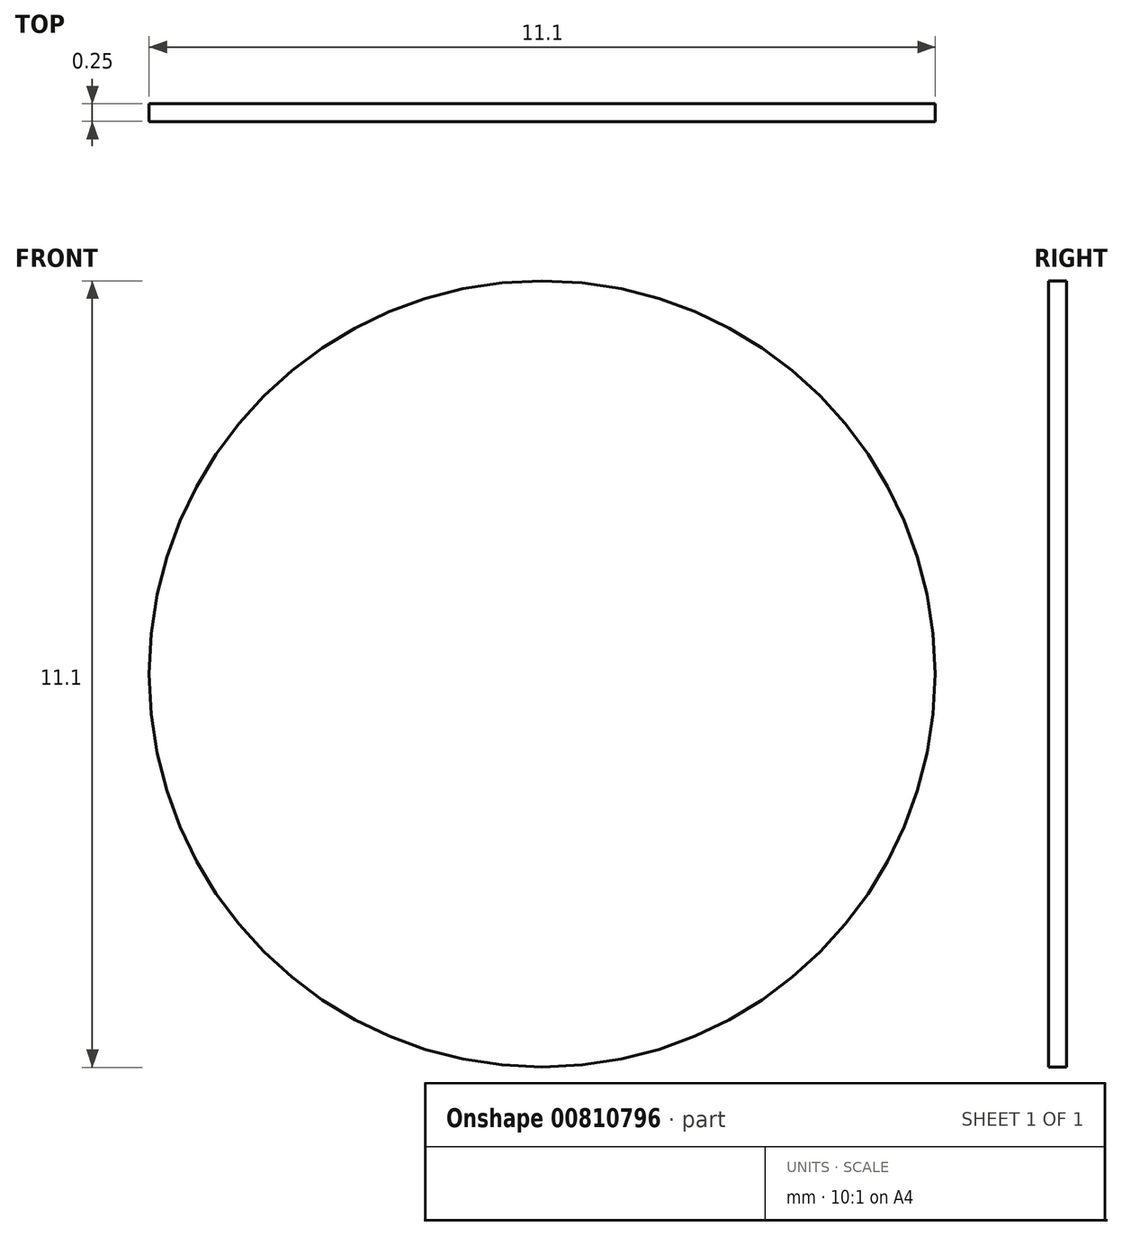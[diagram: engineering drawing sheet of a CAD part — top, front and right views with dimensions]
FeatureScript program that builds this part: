
annotation { "Feature Type Name" : "Feature", "Feature Type Description" : "" }
export const myFeature = defineFeature(function(context is Context, id is Id, definition is map)
    precondition{}
    {
        {
            var Q0;
            Q0=qCreatedBy(makeId("Front.planeOp"),FACE);
            var sketch = newSketch(context, id + "F0", { "sketchPlane" : qUnion([Q0])});
            skCircle(sketch, "E0", {"center": v(-24.15, 20.2) * mm, "radius": 5.55 * mm});
            skSolve(sketch);
        }
        {
            var Q0;
            Q0 = qSketchRegion(id + "F0", true);
            extrude(context, id + "F1", {"entities" : qUnion([Q0]), "depth" : 0.25 * mm, "offsetDistance" : 25.4 * mm});
        }
    });
